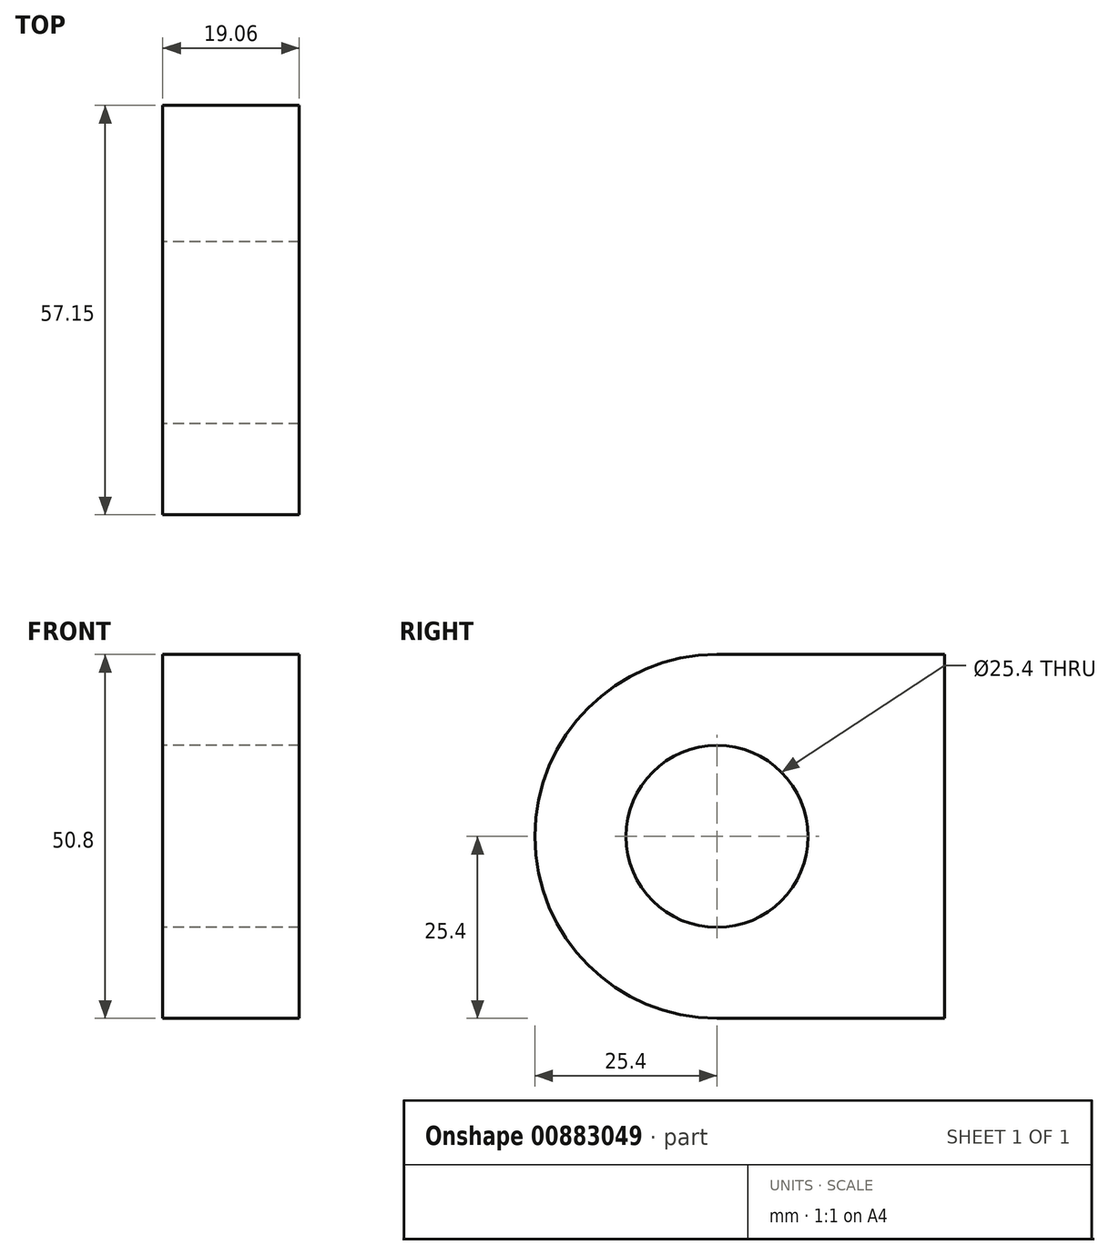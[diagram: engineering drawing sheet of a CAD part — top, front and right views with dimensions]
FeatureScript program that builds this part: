
annotation { "Feature Type Name" : "Feature", "Feature Type Description" : "" }
export const myFeature = defineFeature(function(context is Context, id is Id, definition is map)
    precondition{}
    {
        {
            var Q0;
            Q0=qCreatedBy(makeId("Right.planeOp"),FACE);
            var sketch = newSketch(context, id + "F0", { "sketchPlane" : qUnion([Q0])});
            skCircle(sketch, "E0", {"center": v(0, 0) * mm, "radius": 12.7 * mm});
            skArc(sketch, "E1", {"start": v(0, 25.4) * mm, "mid": v(-25.4, 0) * mm, "end": v(0, -25.4) * mm});
            skLineSegment(sketch, "E2.bottom", {"start": v(0, 25.4) * mm, "end": v(31.75, 25.4) * mm});
            skLineSegment(sketch, "E2.top", {"start": v(0, -25.4) * mm, "end": v(31.75, -25.4) * mm});
            skLineSegment(sketch, "E2.right", {"start": v(31.75, 25.4) * mm, "end": v(31.75, -25.4) * mm});
            skSolve(sketch);
        }
        {
            var Q0;
            Q0=makeQuery(id+"F0.imprint","IMPRINT",FACE,{"disambiguationData":[TD([[makeQuery(id+"F0.imprint","IMPRINT",EDGE,{"derivedFrom":sQuery(id+"F0.wireOp",EDGE,"E0")}),-1.0]])]});
            extrude(context, id + "F1", {"entities" : qUnion([Q0]), "depth" : 19.05 * mm, "symmetric" : true});
        }
    });
